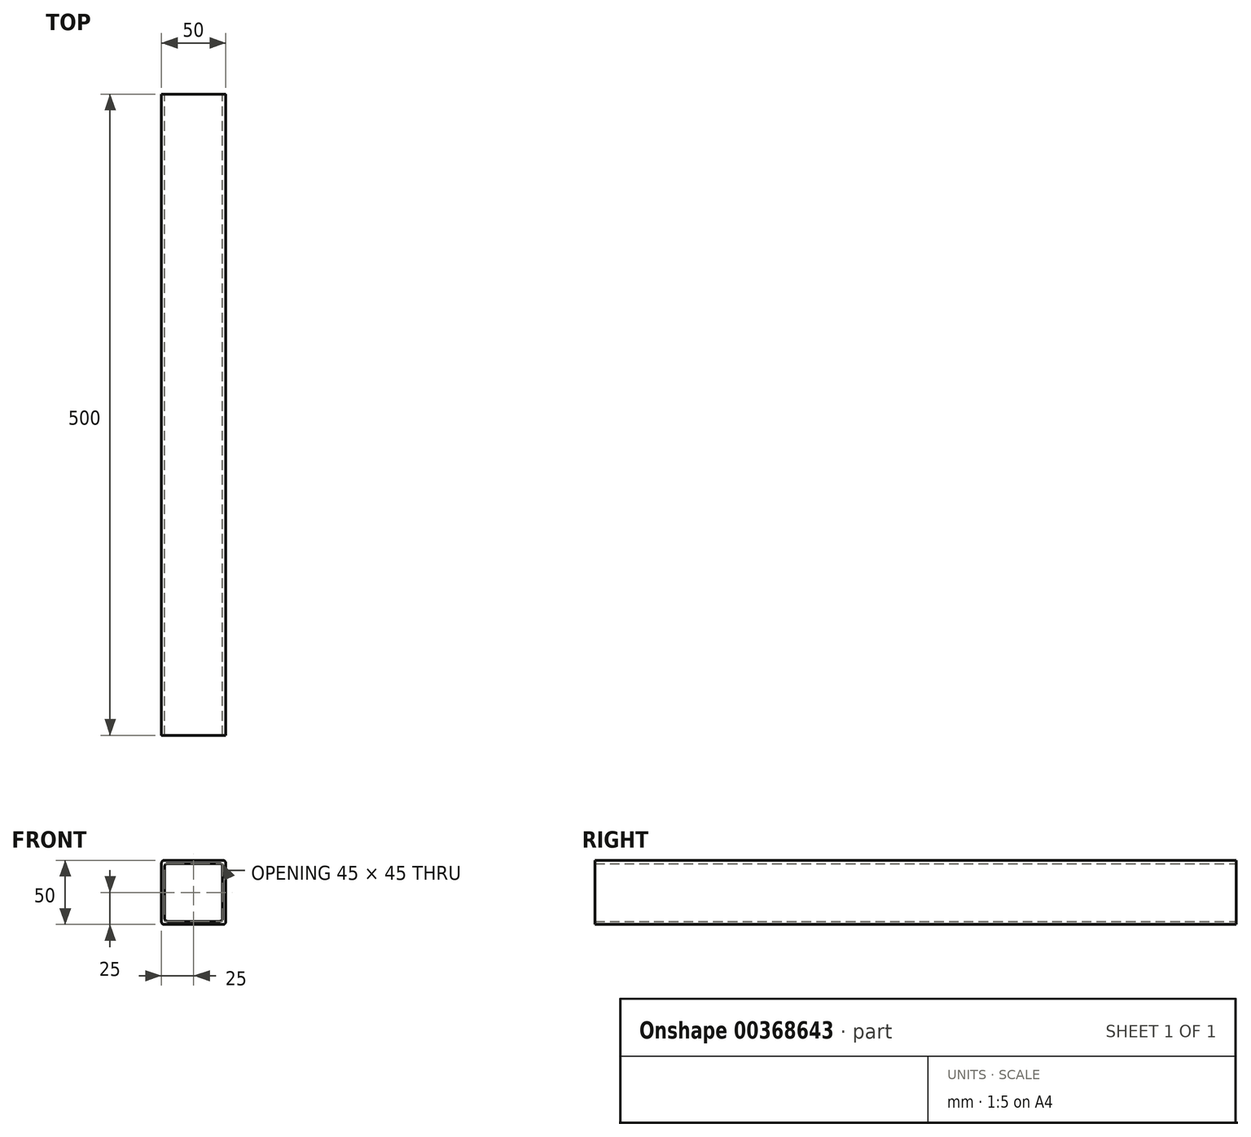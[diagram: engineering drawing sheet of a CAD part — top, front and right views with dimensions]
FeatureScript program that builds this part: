
annotation { "Feature Type Name" : "Feature", "Feature Type Description" : "" }
export const myFeature = defineFeature(function(context is Context, id is Id, definition is map)
    precondition{}
    {
        {
            var Q0;
            Q0=qCreatedBy(makeId("Front.planeOp"),FACE);
            var sketch = newSketch(context, id + "F0", { "sketchPlane" : qUnion([Q0])});
            skLineSegment(sketch, "E0.bottom", {"start": v(23, 25) * mm, "end": v(-23, 25) * mm});
            skLineSegment(sketch, "E0.top", {"start": v(23, -25) * mm, "end": v(-23, -25) * mm});
            skLineSegment(sketch, "E0.left", {"start": v(25, 23) * mm, "end": v(25, -23) * mm});
            skLineSegment(sketch, "E0.right", {"start": v(-25, 23) * mm, "end": v(-25, -23) * mm});
            skPoint(sketch, "E0.middle", {"position": v(0, 0) * mm});
            skLineSegment(sketch, "E1.bottom", {"start": v(20.5, 22.5) * mm, "end": v(-20.5, 22.5) * mm});
            skLineSegment(sketch, "E1.top", {"start": v(20.5, -22.5) * mm, "end": v(-20.5, -22.5) * mm});
            skLineSegment(sketch, "E1.left", {"start": v(22.5, 20.5) * mm, "end": v(22.5, -20.5) * mm});
            skLineSegment(sketch, "E1.right", {"start": v(-22.5, 20.5) * mm, "end": v(-22.5, -20.5) * mm});
            skPoint(sketch, "E2.visualSharp", {"position": v(-25, 25) * mm});
            skArc(sketch, "E2.filletArc", {"start": v(-23, 25) * mm, "mid": v(-24.41, 24.41) * mm, "end": v(-25, 23) * mm});
            skPoint(sketch, "E3.visualSharp", {"position": v(25, 25) * mm});
            skArc(sketch, "E3.filletArc", {"start": v(25, 23) * mm, "mid": v(24.41, 24.41) * mm, "end": v(23, 25) * mm});
            skPoint(sketch, "E4.visualSharp", {"position": v(22.5, 22.5) * mm});
            skArc(sketch, "E4.filletArc", {"start": v(22.5, 20.5) * mm, "mid": v(21.91, 21.91) * mm, "end": v(20.5, 22.5) * mm});
            skPoint(sketch, "E5.visualSharp", {"position": v(-22.5, 22.5) * mm});
            skArc(sketch, "E5.filletArc", {"start": v(-20.5, 22.5) * mm, "mid": v(-21.91, 21.91) * mm, "end": v(-22.5, 20.5) * mm});
            skPoint(sketch, "E6.visualSharp", {"position": v(-22.5, -22.5) * mm});
            skArc(sketch, "E6.filletArc", {"start": v(-22.5, -20.5) * mm, "mid": v(-21.91, -21.91) * mm, "end": v(-20.5, -22.5) * mm});
            skPoint(sketch, "E7.visualSharp", {"position": v(-25, -25) * mm});
            skArc(sketch, "E7.filletArc", {"start": v(-25, -23) * mm, "mid": v(-24.41, -24.41) * mm, "end": v(-23, -25) * mm});
            skPoint(sketch, "E8.visualSharp", {"position": v(22.5, -22.5) * mm});
            skArc(sketch, "E8.filletArc", {"start": v(20.5, -22.5) * mm, "mid": v(21.91, -21.91) * mm, "end": v(22.5, -20.5) * mm});
            skPoint(sketch, "E9.visualSharp", {"position": v(25, -25) * mm});
            skArc(sketch, "E9.filletArc", {"start": v(23, -25) * mm, "mid": v(24.41, -24.41) * mm, "end": v(25, -23) * mm});
            skSolve(sketch);
        }
        {
            var Q0;
            Q0 = qSketchRegion(id + "F0", true);
            extrude(context, id + "F1", {"entities" : qUnion([Q0]), "endBound" : BoundingType.SYMMETRIC, "depth" : 500 * mm});
        }
    });
